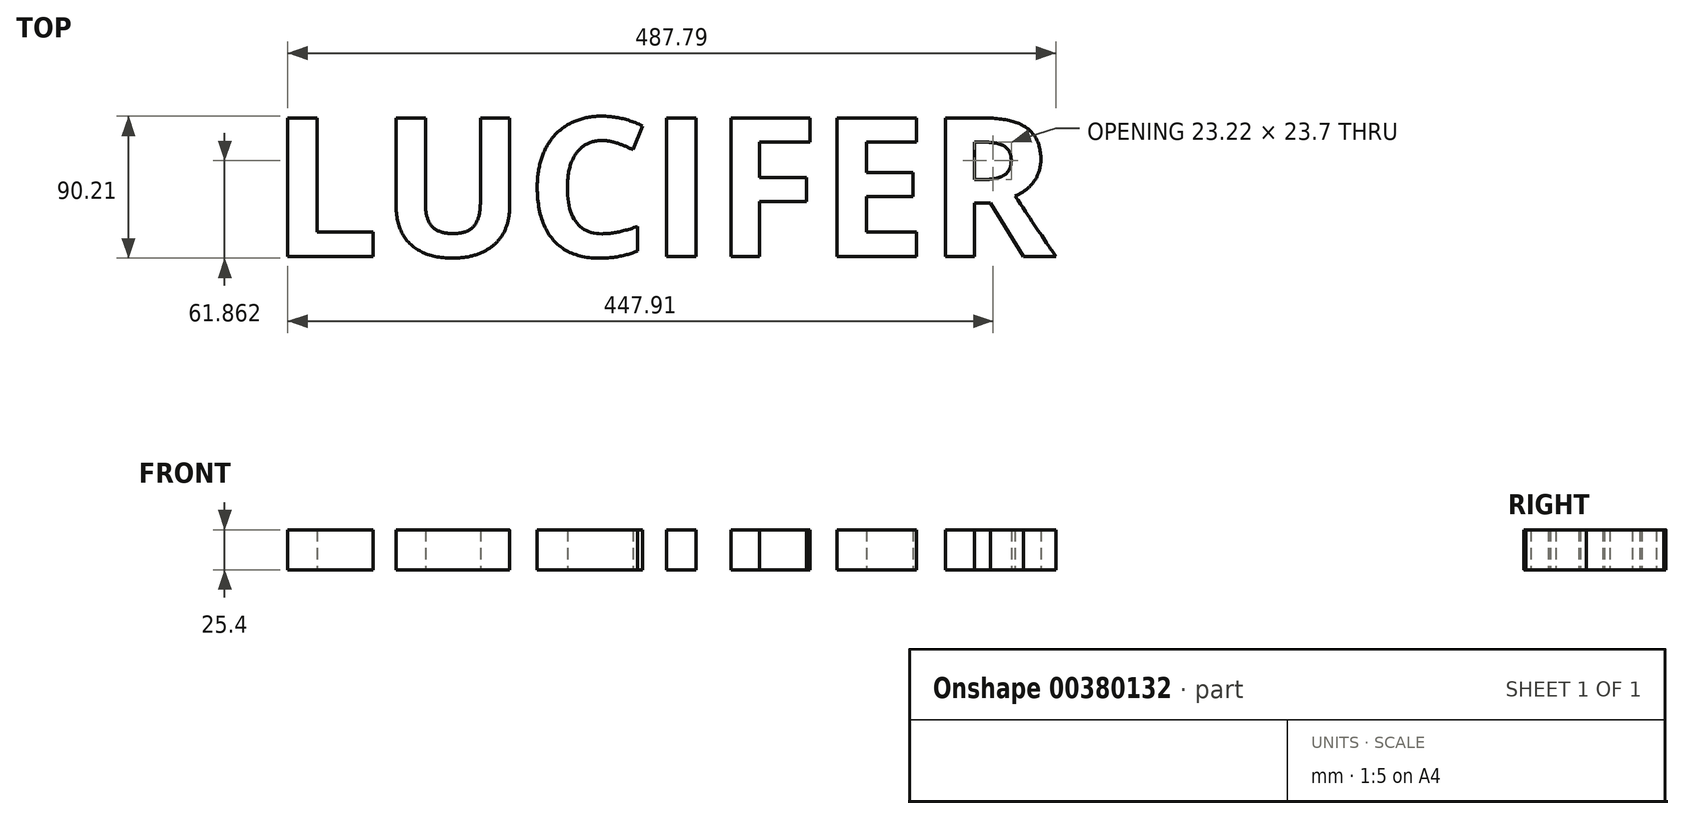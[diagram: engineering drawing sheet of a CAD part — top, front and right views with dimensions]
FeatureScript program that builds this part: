
annotation { "Feature Type Name" : "Feature", "Feature Type Description" : "" }
export const myFeature = defineFeature(function(context is Context, id is Id, definition is map)
    precondition{}
    {
        {
            var Q0;
            Q0=qCreatedBy(makeId("Top.planeOp"),FACE);
            var sketch = newSketch(context, id + "F0", { "sketchPlane" : qUnion([Q0])});
            skText(sketch, "E0", { "text": "LUCIFER", "fontName": "OpenSans-Bold.ttf"});
            const initialGuessF0  = {"E0": [-0.08738, -0.04885, 1, 0, 0.0885]};
            skSetInitialGuess(sketch, initialGuessF0);
            skSolve(sketch);
        }
        {
            var Q0;
            Q0 = qSketchRegion(id + "F0", true);
            extrude(context, id + "F1", {"entities" : qUnion([Q0]), "depth" : 25.4 * mm});
        }
    });
